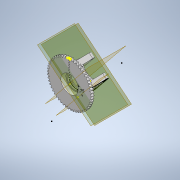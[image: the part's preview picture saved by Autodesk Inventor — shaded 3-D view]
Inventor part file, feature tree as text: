
AUTODESK INVENTOR PART (.ipt)
format: ipt  version: 2022 (Build 260153070, 153G)  size: 672,768 bytes
history: native  units: mm
features: sketch x11, extrude x11, plane x5, mirror x3, loft x2, pattern_circular x1, fillet x1, projected_geometry x1
ambient origin geometry x8: Origin, YZ Plane, XZ Plane, XY Plane, X Axis, Y Axis, Z Axis, Center Point
bodies: Solid1 (feature_tree)
feature tree (35):
  sketch  "Sketch1"  dims[d0=3.0mm d1=0.0mm]
  extrude  "Extrusion1"  TaperAngle=0.0deg  [1 undecoded]
  extrude  "Extrusion2"  Depth=540.0mm TaperAngle=360.0deg
  pattern_circular  "Circular Pattern1"  Count=2  [1 undecoded]
  sketch  "Sketch2"  dims[d2=10.0mm d3=0.0mm d4=540.0mm d5=360.0deg]
  sketch  "Sketch3"  dims[d7=22.5mm]
  extrude  "Extrusion3"  Depth=6.0mm TaperAngle=0.0deg
  sketch  "Sketch4"  dims[d8=3.0mm]
  extrude  "Extrusion4"  Depth=9.5mm TaperAngle=0.0deg
  plane  "Work Plane1"
  extrude  "Extrusion6"  Depth=4.0mm
  plane  "Work Plane2"
  fillet  "Fillet1"  Radius=5.0mm
  loft  "Loft1"
  mirror  "Mirror1"
  plane  "Work Plane6"
  sketch  "Sketch13"  dims[d14=7.5mm d15=0.0mm]
  extrude  "Extrusion7"  TaperAngle=0.0deg  [1 undecoded]
  sketch  "Sketch14"  dims[d16=3.0mm]
  loft  "Loft2"
  sketch  "Sketch15"  dims[d17=1.5mm]
  extrude  "Extrusion12"  TaperAngle=0.0deg  [1 undecoded]
  extrude  "Extrusion9"  Depth=12.5mm TaperAngle=0.0deg
  plane  "Work Plane7"
  mirror  "Mirror2"
  extrude  "Extrusion5"  Depth=2.0mm TaperAngle=0.0deg
  extrude  "Extrusion11"  Depth=24.5mm TaperAngle=0.0deg
  extrude  "Extrusion13"  Depth=25.0mm
  mirror  "Mirror3"
  sketch  "Sketch5"  dims[d9=8.5mm d10=0.0mm]
  sketch  "Sketch7"  dims[d11=1.75mm]
  sketch  "Sketch8"  dims[d12=1.5mm d13=0.0mm]
  projected_geometry  "Projected Loop1"
  plane  "Work Plane8"
  sketch  "Sketch17"  dims[d18=12.0mm d19=20.0mm d20=6.0mm d21=0.0mm d22=9.5mm d23=0.0mm d24=4.0mm d26=5.0mm d27=0.0mm d28=90.0deg d29=0.0mm d30=90.0deg d32=0.0mm d33=90.0deg d34=0.0mm d35=90.0deg d38=12.5mm d39=0.0mm d40=2.0mm d41=0.0mm d44=24.5mm d45=0.0mm d47=25.0mm d48=11.37mm d49=14.0mm d50=2.0mm d51=7.0mm d52=0.0mm d54=1.0mm d55=0.0mm d42=0.5mm d43=0.872665mm]
note: 4 required parameter values undecoded (feature->parameter linkage not recoverable at this tier; creation-order binding heuristic only, values carry confidence <= 0.55)
